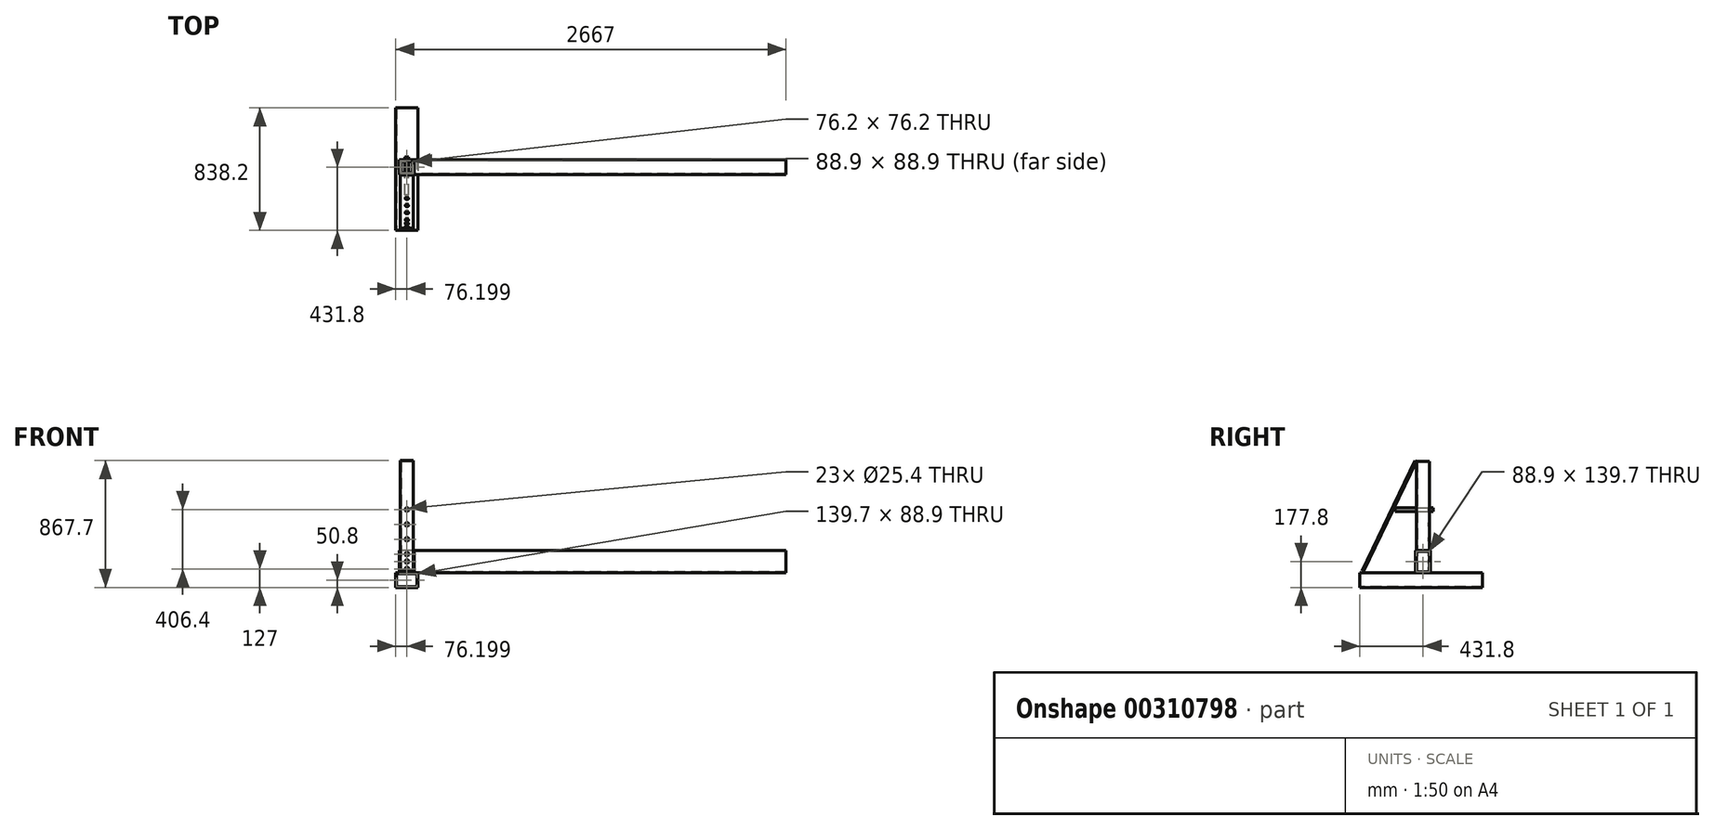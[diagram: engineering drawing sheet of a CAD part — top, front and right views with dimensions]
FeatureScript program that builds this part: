
annotation { "Feature Type Name" : "Feature", "Feature Type Description" : "" }
export const myFeature = defineFeature(function(context is Context, id is Id, definition is map)
    precondition{}
    {
        {
            var Q0;
            Q0=qCreatedBy(makeId("Top.planeOp"),FACE);
            var sketch = newSketch(context, id + "F0", { "sketchPlane" : qUnion([Q0])});
            skLineSegment(sketch, "E0.bottom", {"start": v(-88.51, -50.8) * mm, "end": v(-190.11, -50.8) * mm});
            skLineSegment(sketch, "E0.top", {"start": v(-88.51, 50.8) * mm, "end": v(-190.11, 50.8) * mm});
            skLineSegment(sketch, "E0.left", {"start": v(-88.51, -50.8) * mm, "end": v(-88.51, 50.8) * mm});
            skLineSegment(sketch, "E0.right", {"start": v(-190.11, -50.8) * mm, "end": v(-190.11, 50.8) * mm});
            skPoint(sketch, "E0.middle", {"position": v(-139.31, 0) * mm});
            skLineSegment(sketch, "E1.0", {"start": v(-94.86, 44.45) * mm, "end": v(-183.76, 44.45) * mm});
            skLineSegment(sketch, "E1.1", {"start": v(-94.86, -44.45) * mm, "end": v(-94.86, 44.45) * mm});
            skLineSegment(sketch, "E1.2", {"start": v(-94.86, -44.45) * mm, "end": v(-183.76, -44.45) * mm});
            skLineSegment(sketch, "E1.3", {"start": v(-183.76, -44.45) * mm, "end": v(-183.76, 44.45) * mm});
            skSolve(sketch);
        }
        {
            var Q0;
            Q0=makeQuery(id+"F0.imprint","IMPRINT",FACE,{"disambiguationData":[TD([[makeQuery(id+"F0.imprint","IMPRINT",EDGE,{"derivedFrom":sQuery(id+"F0.wireOp",EDGE,"E0.bottom")}),-1.0]])]});
            extrude(context, id + "F1", {"entities" : qUnion([Q0]), "depth" : 152.4 * mm});
        }
        {
            var Q0;
            Q0=makeQuery(id+"F1.opExtrude","CAP_FACE",FACE,{"disambiguationData":[OSD([sQuery(id+"F0.wireOp",EDGE,"E0.bottom"),sQuery(id+"F0.wireOp",EDGE,"E0.top"),sQuery(id+"F0.wireOp",EDGE,"E0.left"),sQuery(id+"F0.wireOp",EDGE,"E0.right"),sQuery(id+"F0.wireOp",EDGE,"E1.0"),sQuery(id+"F0.wireOp",EDGE,"E1.1"),sQuery(id+"F0.wireOp",EDGE,"E1.2"),sQuery(id+"F0.wireOp",EDGE,"E1.3")])],"isStart":true});
            var sketch = newSketch(context, id + "F2", { "sketchPlane" : qUnion([Q0])});
            skLineSegment(sketch, "E2.0", {"start": v(-101.21, 38.1) * mm, "end": v(-101.21, -38.1) * mm});
            skLineSegment(sketch, "E2.1", {"start": v(-101.21, 38.1) * mm, "end": v(-177.41, 38.1) * mm});
            skLineSegment(sketch, "E2.2", {"start": v(-177.41, 38.1) * mm, "end": v(-177.41, -38.1) * mm});
            skLineSegment(sketch, "E2.3", {"start": v(-101.21, -38.1) * mm, "end": v(-177.41, -38.1) * mm});
            skSolve(sketch);
        }
        {
            var Q0;
            Q0=makeQuery(id+"F2.imprint","IMPRINT",FACE,{"disambiguationData":[TD([[makeQuery(id+"F2.imprint","IMPRINT",EDGE,{"derivedFrom":sQuery(id+"F2.wireOp",EDGE,"E2.0")}),1.0]])]});
            extrude(context, id + "F3", {"entities" : qUnion([Q0]), "oppositeDirection" : true, "depth" : 762 * mm});
        }
        {
            var Q0;
            Q0=makeQuery(id+"F1.opExtrude","SWEPT_FACE",FACE,{"disambiguationData":[OSD([sQuery(id+"F0.wireOp",EDGE,"E0.left")])]});
            var sketch = newSketch(context, id + "F4", { "sketchPlane" : qUnion([Q0])});
            skLineSegment(sketch, "E3.0", {"start": v(44.45, 146.05) * mm, "end": v(44.45, 6.35) * mm});
            skLineSegment(sketch, "E3.1", {"start": v(-44.45, 146.05) * mm, "end": v(44.45, 146.05) * mm});
            skLineSegment(sketch, "E3.2", {"start": v(-44.45, 146.05) * mm, "end": v(-44.45, 6.35) * mm});
            skLineSegment(sketch, "E3.3", {"start": v(-44.45, 6.35) * mm, "end": v(44.45, 6.35) * mm});
            skSolve(sketch);
        }
        {
            var Q0;
            Q0=makeQuery(id+"F4.imprint","IMPRINT",FACE,{"disambiguationData":[TD([[makeQuery(id+"F4.imprint","IMPRINT",EDGE,{"derivedFrom":sQuery(id+"F4.wireOp",EDGE,"E3.0")}),1.0]])]});
            extrude(context, id + "F5", {"entities" : qUnion([Q0]), "depth" : 2540 * mm});
        }
        {
            var Q0;
            Q0=makeQuery(id+"F1.opExtrude","SWEPT_FACE",FACE,{"disambiguationData":[OSD([sQuery(id+"F0.wireOp",EDGE,"E0.bottom")])]});
            cPlane(context, id + "F6", {"entities" : qUnion([Q0]), "cplaneType" : CPlaneType.OFFSET, "offset" : 381 * mm, "width" : 152.4 * mm, "height" : 152.4 * mm});
        }
        {
            var Q0;
            Q0=qCreatedBy(id+"F6.planeOp",FACE);
            var sketch = newSketch(context, id + "F7", { "sketchPlane" : qUnion([Q0])});
            skLineSegment(sketch, "E4", {"start": v(-215.51, 0) * mm, "end": v(-215.51, -101.6) * mm});
            skLineSegment(sketch, "E5", {"start": v(-215.51, -101.6) * mm, "end": v(-63.11, -101.6) * mm});
            skLineSegment(sketch, "E6", {"start": v(-63.11, -101.6) * mm, "end": v(-63.11, 0) * mm});
            skLineSegment(sketch, "E7", {"start": v(-63.11, 0) * mm, "end": v(-215.51, 0) * mm});
            skLineSegment(sketch, "E8.0", {"start": v(-69.46, -95.25) * mm, "end": v(-69.46, -6.35) * mm});
            skLineSegment(sketch, "E8.1", {"start": v(-209.16, -95.25) * mm, "end": v(-69.46, -95.25) * mm});
            skLineSegment(sketch, "E8.2", {"start": v(-209.16, -6.35) * mm, "end": v(-209.16, -95.25) * mm});
            skLineSegment(sketch, "E8.3", {"start": v(-69.46, -6.35) * mm, "end": v(-209.16, -6.35) * mm});
            skSolve(sketch);
        }
        {
            var Q0;
            Q0 = qSketchRegion(id + "F7", true);
            extrude(context, id + "F8", {"entities" : qUnion([Q0]), "oppositeDirection" : true, "depth" : 838.2 * mm});
        }
        {
            var Q0;
            Q0=makeQuery(id+"F3.opExtrude","SWEPT_FACE",FACE,{"disambiguationData":[OSD([sQuery(id+"F0.wireOp",EDGE,"E1.3")])]});
            var sketch = newSketch(context, id + "F9", { "sketchPlane" : qUnion([Q0])});
            skLineSegment(sketch, "E9", {"start": v(44.45, 762) * mm, "end": v(428, 0) * mm});
            skSolve(sketch);
        }
        {
            var Q0;
            {var subQ0=sQuery(id+"F0.wireOp",EDGE,"E1.3");Q0=makeQuery(id+"F9.imprint","IMPRINT",FACE,{"disambiguationData":[TD([[makeQuery(id+"F9.imprint","IMPRINT",EDGE,{"derivedFrom":makeQuery(id+"F3.opExtrude","CAP_EDGE",EDGE,{"disambiguationData":[OSD([subQ0])],"isStart":true})}),-1.0]])]});}
            var sketch = newSketch(context, id + "F10", { "sketchPlane" : qUnion([Q0])});
            skLineSegment(sketch, "E10", {"start": v(44.83, 762.15) * mm, "end": v(-18.25, 731.76) * mm});
            skSolve(sketch);
        }
        {
            var Q0;
            Q0=makeQuery(id+"F3.opExtrude","SWEPT_FACE",FACE,{"disambiguationData":[OSD([sQuery(id+"F0.wireOp",EDGE,"E1.2")])]});
            var Q1;
            Q1=sQuery(id+"F10.wireOp",EDGE,"E10");
            cPlane(context, id + "F11", {"entities" : qUnion([Q0, Q1]), "cplaneType" : CPlaneType.LINE_ANGLE, "offset" : 25.4 * mm, "angle" : 0 * degree, "width" : 152.4 * mm, "height" : 152.4 * mm});
        }
        {
            var Q0;
            Q0=qCreatedBy(id+"F11.planeOp",FACE);
            var sketch = newSketch(context, id + "F12", { "sketchPlane" : qUnion([Q0])});
            skLineSegment(sketch, "E11", {"start": v(-183.92, -370.71) * mm, "end": v(-95.02, -370.71) * mm});
            skLineSegment(sketch, "E12", {"start": v(-95.02, -370.71) * mm, "end": v(-95.02, -380.24) * mm});
            skLineSegment(sketch, "E13", {"start": v(-95.02, -380.24) * mm, "end": v(-183.92, -380.24) * mm});
            skLineSegment(sketch, "E14", {"start": v(-183.92, -380.24) * mm, "end": v(-183.92, -370.71) * mm});
            skSolve(sketch);
        }
        {
            var Q0;
            Q0 = qSketchRegion(id + "F12", true);
            extrude(context, id + "F13", {"entities" : qUnion([Q0]), "oppositeDirection" : true, "depth" : 838.2 * mm});
        }
        {
            var Q0;
            {var subQ0=sQuery(id+"F0.wireOp",EDGE,"E0.top");Q0=makeQuery(id+"FShHTiWVJbrXebT_5.boolean.opBoolean","MERGE",FACE,{"derivedFrom":[makeQuery(id+"F1.opExtrude","SWEPT_FACE",FACE,{"disambiguationData":[OSD([subQ0])]}),makeQuery(id+"FShHTiWVJbrXebT_5.opExtrude","SWEPT_FACE",FACE,{"disambiguationData":[OSD([subQ0])]})]});}
            var sketch = newSketch(context, id + "F14", { "sketchPlane" : qUnion([Q0])});
            skCircle(sketch, "E15", {"center": v(139.31, 25.4) * mm, "radius": 12.7 * mm});
            skPoint(sketch, "E15.centerSnap0", {"position": v(139.31, 0) * mm});
            skSolve(sketch);
        }
        {
            var Q0;
            Q0=makeQuery(id+"F14.imprint","IMPRINT",FACE,{"disambiguationData":[TD([[makeQuery(id+"F14.imprint","IMPRINT",EDGE,{"derivedFrom":sQuery(id+"F14.wireOp",EDGE,"E15")}),1.0]])]});
            extrude(context, id + "F15", {"entities" : qUnion([Q0]), "operationType" : NewBodyOperationType.REMOVE, "endBound" : BoundingType.THROUGH_ALL, "oppositeDirection" : true, "depth" : 25.4 * mm});
        }
        {
            var Q0;
            Q0=makeQuery(id+"F3.opExtrude","SWEPT_FACE",FACE,{"disambiguationData":[OSD([sQuery(id+"F0.wireOp",EDGE,"E1.0")])]});
            var sketch = newSketch(context, id + "F16", { "sketchPlane" : qUnion([Q0])});
            skCircle(sketch, "E16", {"center": v(139.31, 431.8) * mm, "radius": 12.7 * mm});
            skPoint(sketch, "E16.centerSnap0", {"position": v(139.31, 762) * mm});
            skCircle(sketch, "E17.0.1.0", {"center": v(139.31, 330.2) * mm, "radius": 12.7 * mm});
            skCircle(sketch, "E17.0.2.0", {"center": v(139.31, 228.6) * mm, "radius": 12.7 * mm});
            skCircle(sketch, "E17.0.3.0", {"center": v(139.31, 127) * mm, "radius": 12.7 * mm});
            skLineSegment(sketch, "E17.direction1", {"start": v(139.31, 431.8) * mm, "end": v(164.71, 431.8) * mm, "construction": true});
            skLineSegment(sketch, "E17.direction2", {"start": v(139.31, 431.8) * mm, "end": v(139.31, 330.2) * mm, "construction": true});
            skSolve(sketch);
        }
        {
            var Q0;
            Q0=makeQuery(id+"F16.imprint","IMPRINT",FACE,{"disambiguationData":[TD([[makeQuery(id+"F16.imprint","IMPRINT",EDGE,{"derivedFrom":sQuery(id+"F16.wireOp",EDGE,"E16")}),1.0]])]});
            var Q1;
            Q1=makeQuery(id+"F16.imprint","IMPRINT",FACE,{"disambiguationData":[TD([[makeQuery(id+"F16.imprint","IMPRINT",EDGE,{"derivedFrom":sQuery(id+"F16.wireOp",EDGE,"E17.0.1.0")}),1.0]])]});
            var Q2;
            Q2=makeQuery(id+"F16.imprint","IMPRINT",FACE,{"disambiguationData":[TD([[makeQuery(id+"F16.imprint","IMPRINT",EDGE,{"derivedFrom":sQuery(id+"F16.wireOp",EDGE,"E17.0.2.0")}),1.0]])]});
            var Q3;
            Q3=makeQuery(id+"F16.imprint","IMPRINT",FACE,{"disambiguationData":[TD([[makeQuery(id+"F16.imprint","IMPRINT",EDGE,{"derivedFrom":sQuery(id+"F16.wireOp",EDGE,"E17.0.3.0")}),1.0]])]});
            extrude(context, id + "F17", {"entities" : qUnion([Q0, Q1, Q2, Q3]), "operationType" : NewBodyOperationType.REMOVE, "endBound" : BoundingType.THROUGH_ALL, "oppositeDirection" : true, "depth" : 25.4 * mm});
        }
        {
            var Q0;
            Q0=makeQuery(id+"F16.imprint","IMPRINT",FACE,{"disambiguationData":[TD([[makeQuery(id+"F16.imprint","IMPRINT",EDGE,{"derivedFrom":sQuery(id+"F16.wireOp",EDGE,"E16")}),1.0]])]});
            extrude(context, id + "F18", {"entities" : qUnion([Q0]), "oppositeDirection" : true, "depth" : 233.68 * mm, "hasSecondDirection" : true, "secondDirectionOppositeDirection" : false, "secondDirectionDepth" : 25.4 * mm});
        }
        {
            var Q0;
            Q0=makeQuery(id+"F1.opExtrude","SWEPT_FACE",FACE,{"disambiguationData":[OSD([sQuery(id+"F0.wireOp",EDGE,"E0.top")])]});
            var sketch = newSketch(context, id + "F19", { "sketchPlane" : qUnion([Q0])});
            skCircle(sketch, "E18", {"center": v(139.31, 76.2) * mm, "radius": 12.7 * mm});
            skPoint(sketch, "E18.centerSnap0", {"position": v(139.31, 0) * mm});
            skSolve(sketch);
        }
        {
            var Q0;
            Q0 = qSketchRegion(id + "F19", true);
            extrude(context, id + "F20", {"entities" : qUnion([Q0]), "operationType" : NewBodyOperationType.REMOVE, "endBound" : BoundingType.THROUGH_ALL, "oppositeDirection" : true, "depth" : 25.4 * mm});
        }
    });
